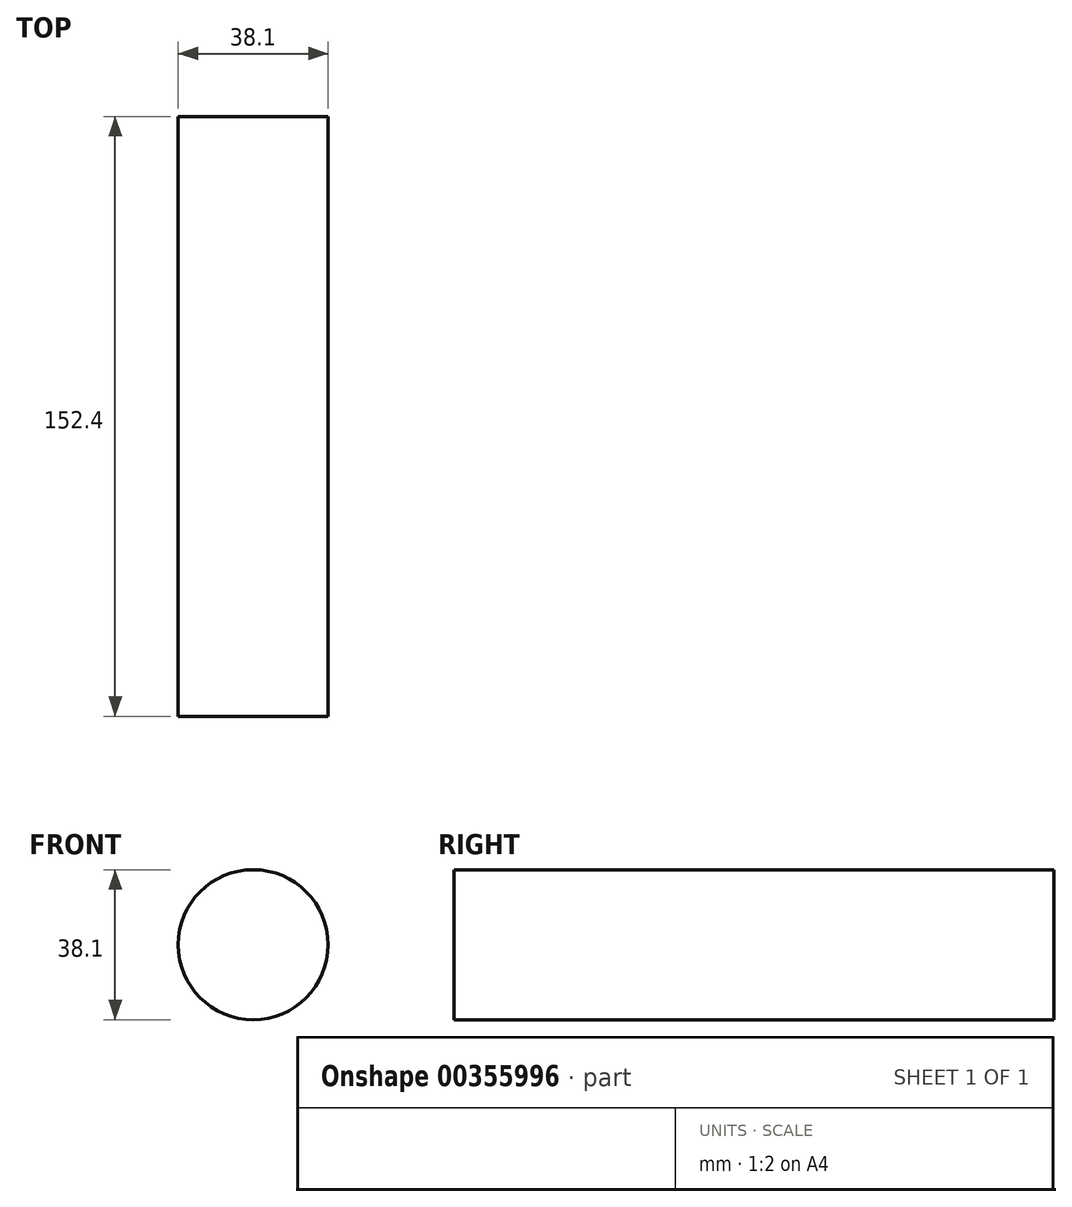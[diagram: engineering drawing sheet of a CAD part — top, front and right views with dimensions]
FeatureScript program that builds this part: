
annotation { "Feature Type Name" : "Feature", "Feature Type Description" : "" }
export const myFeature = defineFeature(function(context is Context, id is Id, definition is map)
    precondition{}
    {
        {
            var Q0;
            Q0=qCreatedBy(makeId("Front.planeOp"),FACE);
            var sketch = newSketch(context, id + "F0", { "sketchPlane" : qUnion([Q0])});
            skCircle(sketch, "E0", {"center": v(0, 0) * mm, "radius": 19.05 * mm});
            skSolve(sketch);
        }
        {
            var Q0;
            Q0=qSketchRegion(id+"F0",true);
            extrude(context, id + "F1", {"entities" : qUnion([Q0]), "depth" : 152.4 * mm});
        }
    });
